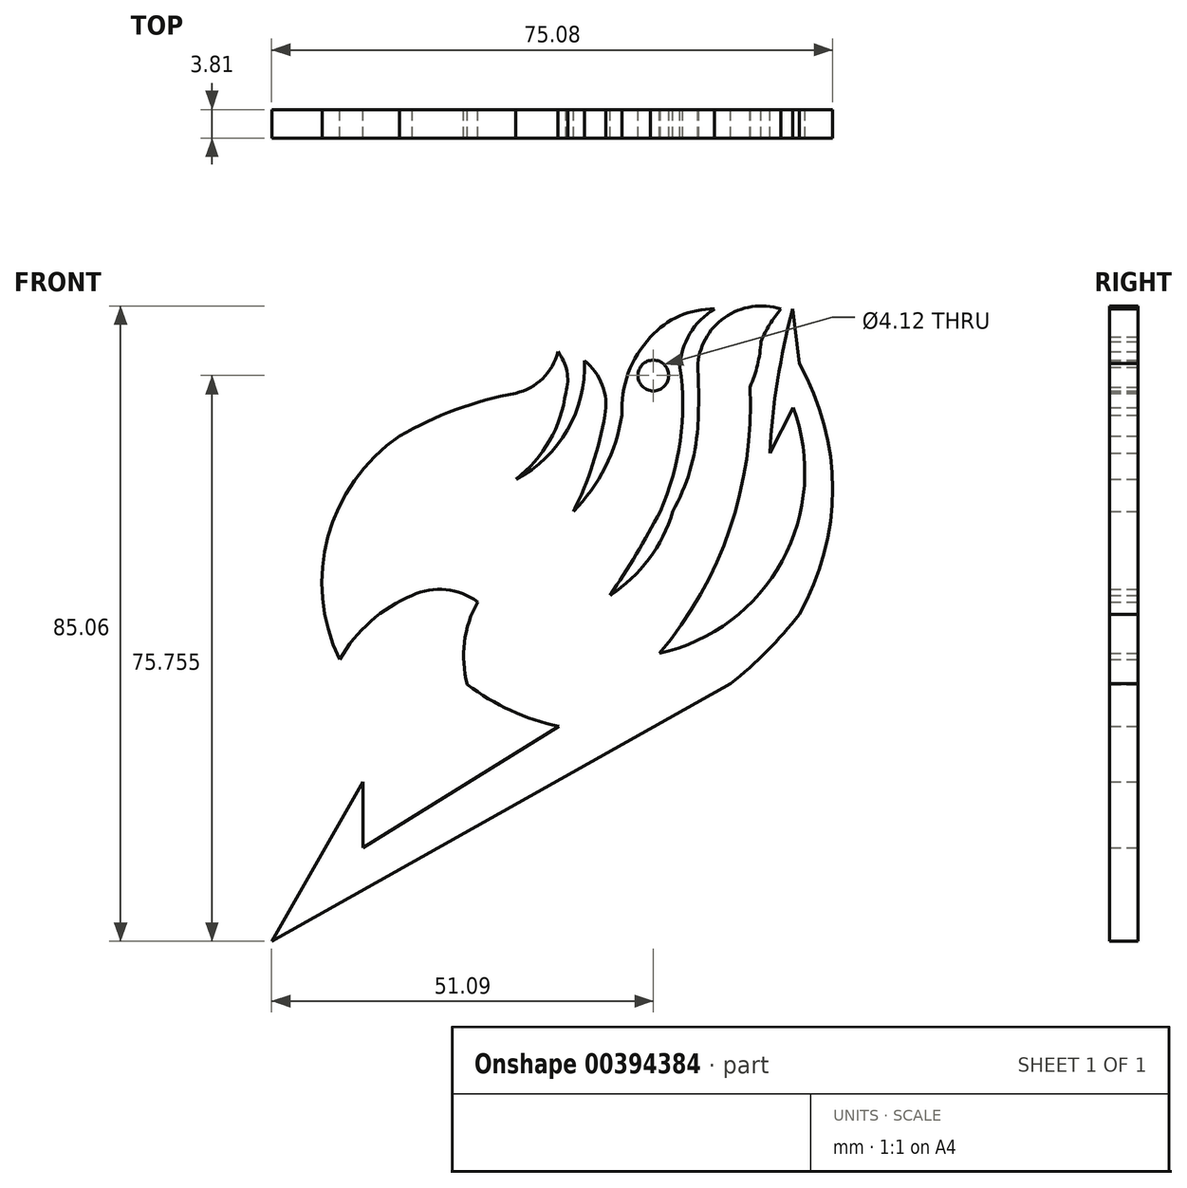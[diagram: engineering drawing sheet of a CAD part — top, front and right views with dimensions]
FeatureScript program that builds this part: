
annotation { "Feature Type Name" : "Feature", "Feature Type Description" : "" }
export const myFeature = defineFeature(function(context is Context, id is Id, definition is map)
    precondition{}
    {
        {
            var Q0;
            Q0=qCreatedBy(makeId("Front.planeOp"),FACE);
            var sketch = newSketch(context, id + "F0", { "sketchPlane" : qUnion([Q0])});
            skArc(sketch, "E0", {"start": v(-22.23, 26.74) * mm, "mid": v(-31.83, 13.27) * mm, "end": v(-30.27, -3.2) * mm});
            skArc(sketch, "E1", {"start": v(-6.73, 32.48) * mm, "mid": v(-14.72, 30.26) * mm, "end": v(-22.23, 26.74) * mm});
            skArc(sketch, "E2", {"start": v(-6.73, 32.48) * mm, "mid": v(-3.1, 34.44) * mm, "end": v(-1.05, 38) * mm});
            skArc(sketch, "E3", {"start": v(0, 32.6) * mm, "mid": v(0.15, 35.43) * mm, "end": v(-1.05, 38) * mm});
            skArc(sketch, "E4", {"start": v(-6.67, 20.97) * mm, "mid": v(-2.17, 26.11) * mm, "end": v(0, 32.6) * mm});
            skArc(sketch, "E5", {"start": v(-6.67, 20.97) * mm, "mid": v(0.24, 27.55) * mm, "end": v(2.5, 36.83) * mm});
            skArc(sketch, "E6", {"start": v(5.25, 29.54) * mm, "mid": v(4.88, 33.56) * mm, "end": v(2.5, 36.83) * mm});
            skArc(sketch, "E7", {"start": v(1.02, 16.63) * mm, "mid": v(3.61, 22.93) * mm, "end": v(5.25, 29.54) * mm});
            skArc(sketch, "E8", {"start": v(1.02, 16.63) * mm, "mid": v(5.28, 22.57) * mm, "end": v(7.52, 29.54) * mm});
            skArc(sketch, "E9", {"start": v(11.36, 39.98) * mm, "mid": v(8.37, 35.15) * mm, "end": v(7.52, 29.54) * mm});
            skArc(sketch, "E10", {"start": v(19.93, 43.72) * mm, "mid": v(15.23, 42.8) * mm, "end": v(11.36, 39.98) * mm});
            skArc(sketch, "E11", {"start": v(19.93, 43.72) * mm, "mid": v(16.61, 40.43) * mm, "end": v(15.3, 35.94) * mm});
            skArc(sketch, "E12", {"start": v(12.64, 16.63) * mm, "mid": v(15.3, 26.1) * mm, "end": v(15.3, 35.94) * mm});
            skArc(sketch, "E13", {"start": v(5.94, 5.4) * mm, "mid": v(9.44, 10.93) * mm, "end": v(12.64, 16.63) * mm});
            skArc(sketch, "E14", {"start": v(5.94, 5.4) * mm, "mid": v(11.13, 10.27) * mm, "end": v(14.31, 16.63) * mm});
            skArc(sketch, "E15", {"start": v(14.31, 16.63) * mm, "mid": v(16.6, 22.06) * mm, "end": v(17.66, 27.86) * mm});
            skArc(sketch, "E16", {"start": v(28.8, 43.72) * mm, "mid": v(21.28, 42.61) * mm, "end": v(17.66, 35.94) * mm});
            skArc(sketch, "E17", {"start": v(17.66, 27.86) * mm, "mid": v(17.8, 31.9) * mm, "end": v(17.66, 35.94) * mm});
            skArc(sketch, "E18", {"start": v(28.8, 43.72) * mm, "mid": v(27.3, 41.66) * mm, "end": v(26.15, 39.39) * mm});
            skArc(sketch, "E19", {"start": v(24.67, 33.28) * mm, "mid": v(25.67, 36.27) * mm, "end": v(26.15, 39.39) * mm});
            skArc(sketch, "E20", {"start": v(12.54, -2.38) * mm, "mid": v(21.97, 14.3) * mm, "end": v(24.67, 33.28) * mm});
            skArc(sketch, "E21", {"start": v(12.54, -2.38) * mm, "mid": v(28.97, 10) * mm, "end": v(30.47, 30.52) * mm});
            skLineSegment(sketch, "E22", {"start": v(30.47, 30.52) * mm, "end": v(27.31, 24.42) * mm});
            skArc(sketch, "E23", {"start": v(30.37, 43.72) * mm, "mid": v(28.35, 34.15) * mm, "end": v(27.31, 24.42) * mm});
            skLineSegment(sketch, "E24", {"start": v(30.37, 43.72) * mm, "end": v(31.25, 36.43) * mm});
            skArc(sketch, "E25", {"start": v(31.25, 2.84) * mm, "mid": v(35.7, 19.64) * mm, "end": v(31.25, 36.43) * mm});
            skArc(sketch, "E26", {"start": v(22.1, -6.42) * mm, "mid": v(26.95, -2.06) * mm, "end": v(31.25, 2.84) * mm});
            skLineSegment(sketch, "E27", {"start": v(22.1, -6.42) * mm, "end": v(-39.37, -40.92) * mm});
            skLineSegment(sketch, "E28", {"start": v(-39.37, -40.92) * mm, "end": v(-27.15, -19.53) * mm});
            skLineSegment(sketch, "E29", {"start": v(-27.15, -19.53) * mm, "end": v(-27.15, -28.4) * mm});
            skLineSegment(sketch, "E30", {"start": v(-27.15, -28.4) * mm, "end": v(-0.95, -12.14) * mm});
            skArc(sketch, "E31", {"start": v(-13.17, -6.52) * mm, "mid": v(-7.37, -10) * mm, "end": v(-0.95, -12.14) * mm});
            skArc(sketch, "E32", {"start": v(-11.79, 4.52) * mm, "mid": v(-13.57, -0.86) * mm, "end": v(-13.17, -6.52) * mm});
            skArc(sketch, "E33", {"start": v(-11.79, 4.52) * mm, "mid": v(-16.05, 6.19) * mm, "end": v(-20.56, 5.4) * mm});
            skArc(sketch, "E34", {"start": v(-20.56, 5.4) * mm, "mid": v(-26.12, 1.91) * mm, "end": v(-30.27, -3.2) * mm});
            skCircle(sketch, "E35", {"center": v(11.72, 34.83) * mm, "radius": 2.06 * mm});
            skSolve(sketch);
        }
        {
            var Q0;
            Q0 = qSketchRegion(id + "F0", true);
            extrude(context, id + "F1", {"entities" : qUnion([Q0]), "depth" : 3.8 * mm});
        }
    });
